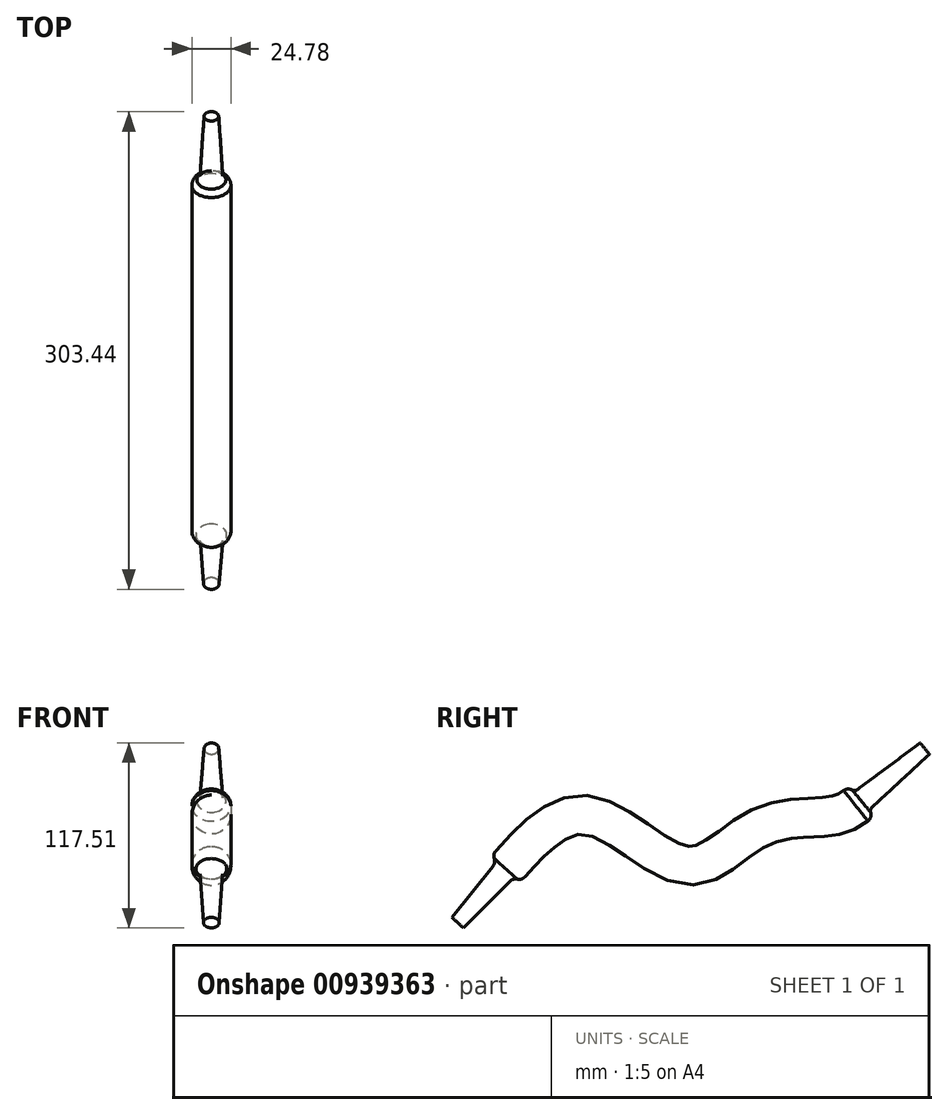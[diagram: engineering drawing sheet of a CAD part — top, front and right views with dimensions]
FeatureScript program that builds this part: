
annotation { "Feature Type Name" : "Feature", "Feature Type Description" : "" }
export const myFeature = defineFeature(function(context is Context, id is Id, definition is map)
    precondition{}
    {
        {
            var Q0;
            Q0=qCreatedBy(makeId("Right.planeOp"),FACE);
            var sketch = newSketch(context, id + "F0", { "sketchPlane" : qUnion([Q0])});
            skFitSpline(sketch, "E0", {"points": [v(-105.94, 7.66) * mm, v(-52.75, 42.35) * mm, v(10.26, 10.26) * mm, v(57.1, 35.12) * mm, v(104.5, 42.35) * mm, v(120.69, 51.3) * mm], "startDerivative": vector(221.57, 247.6) * mm, "endDerivative": vector(107.5, 89.11) * mm});
            skSolve(sketch);
        }
        {
            var Q0;
            Q0=sQuery(id+"F0.wireOp",EDGE,"E0");
            var Q1;
            Q1=sQuery(id+"F0.wireOp",VERTEX,"E0.start");
            cPlane(context, id + "F1", {"entities" : qUnion([Q0, Q1]), "cplaneType" : CPlaneType.CURVE_POINT, "offset" : 25 * mm, "width" : 150 * mm, "height" : 150 * mm});
        }
        {
            var Q0;
            Q0=qCreatedBy(id+"F1.planeOp",FACE);
            var sketch = newSketch(context, id + "F2", { "sketchPlane" : qUnion([Q0])});
            skCircle(sketch, "E1", {"center": v(0, -83.82) * mm, "radius": 12.39 * mm});
            skSolve(sketch);
        }
        {
            var Q0;
            Q0=makeQuery(id+"F2.imprint","IMPRINT",FACE,{"disambiguationData":[TD([[makeQuery(id+"F2.imprint","IMPRINT",EDGE,{"derivedFrom":sQuery(id+"F2.wireOp",EDGE,"E1")}),1.0]])]});
            var Q1;
            Q1=sQuery(id+"F0.wireOp",EDGE,"E0");
            sweep(context, id + "F3", {"profiles" : qUnion([Q0]), "path" : qUnion([Q1])});
        }
        {
            var Q0;
            Q0=makeQuery(id+"F3.opSweep","CAP_EDGE",EDGE,{"disambiguationData":[OSD([sQuery(id+"F0.wireOp",VERTEX,"E0.start"),sQuery(id+"F2.wireOp",EDGE,"E1")])],"isStart":true});
            var Q1;
            Q1=makeQuery(id+"F3.opSweep","CAP_EDGE",EDGE,{"disambiguationData":[OSD([sQuery(id+"F0.wireOp",VERTEX,"E0.end"),sQuery(id+"F2.wireOp",EDGE,"E1")])],"isStart":false});
            fillet(context, id + "F4", {"entities" : qUnion([Q0, Q1]), "radius" : 5 * mm, "tangentPropagation" : true, "allowEdgeOverflow" : false});
        }
        {
            var Q0;
            Q0=makeQuery(id+"F3.opSweep","CAP_FACE",FACE,{"disambiguationData":[OSD([sQuery(id+"F0.wireOp",VERTEX,"E0.start"),sQuery(id+"F2.wireOp",EDGE,"E1")])],"isStart":true});
            extrude(context, id + "F5", {"entities" : qUnion([Q0]), "operationType" : NewBodyOperationType.ADD, "depth" : 45.2 * mm, "offsetDistance" : 25 * mm, "hasDraft" : true, "draftAngle" : 3 * degree, "draftPullDirection" : true});
        }
        {
            var Q0;
            {var subQ0=sQuery(id+"F2.wireOp",EDGE,"E1");var subQ1=sQuery(id+"F0.wireOp",VERTEX,"E0.start");Q0=makeQuery(id+"F5.boolean.opBoolean","MERGE",EDGE,{"derivedFrom":[makeQuery(id+"F4.opFillet","BLEND_EDGE",EDGE,{"blendedFrom":[makeQuery(id+"F3.opSweep","CAP_EDGE",EDGE,{"disambiguationData":[OSD([subQ1,subQ0])],"isStart":true}),makeQuery(id+"F3.opSweep","CAP_FACE",FACE,{"disambiguationData":[OSD([subQ1,subQ0])],"isStart":true})],"blendedInto":[makeQuery(id+"F3.opSweep","CAP_FACE",FACE,{"disambiguationData":[OSD([subQ1,subQ0])],"isStart":true})]}),makeQuery(id+"F5.opExtrude","CAP_EDGE",EDGE,{"disambiguationData":[OSD([subQ1,subQ0])],"isStart":true})]});}
            fillet(context, id + "F6", {"entities" : qUnion([Q0]), "radius" : 5 * mm, "tangentPropagation" : true, "allowEdgeOverflow" : false});
        }
        {
            var Q0;
            Q0=makeQuery(id+"F3.opSweep","CAP_FACE",FACE,{"disambiguationData":[OSD([sQuery(id+"F0.wireOp",VERTEX,"E0.end"),sQuery(id+"F2.wireOp",EDGE,"E1")])],"isStart":false});
            extrude(context, id + "F7", {"entities" : qUnion([Q0]), "operationType" : NewBodyOperationType.ADD, "depth" : 52 * mm, "offsetDistance" : 25 * mm, "hasDraft" : true, "draftAngle" : 3 * degree, "draftPullDirection" : true});
        }
        {
            var Q0;
            {var subQ0=sQuery(id+"F2.wireOp",EDGE,"E1");var subQ1=sQuery(id+"F0.wireOp",VERTEX,"E0.end");Q0=makeQuery(id+"F7.boolean.opBoolean","MERGE",EDGE,{"derivedFrom":[makeQuery(id+"F4.opFillet","BLEND_EDGE",EDGE,{"blendedFrom":[makeQuery(id+"F3.opSweep","CAP_EDGE",EDGE,{"disambiguationData":[OSD([subQ1,subQ0])],"isStart":false}),makeQuery(id+"F3.opSweep","CAP_FACE",FACE,{"disambiguationData":[OSD([subQ1,subQ0])],"isStart":false})],"blendedInto":[makeQuery(id+"F3.opSweep","CAP_FACE",FACE,{"disambiguationData":[OSD([subQ1,subQ0])],"isStart":false})]}),makeQuery(id+"F7.opExtrude","CAP_EDGE",EDGE,{"disambiguationData":[OSD([subQ1,subQ0])],"isStart":true})]});}
            fillet(context, id + "F8", {"entities" : qUnion([Q0]), "radius" : 3 * mm, "tangentPropagation" : true, "allowEdgeOverflow" : false});
        }
    });
